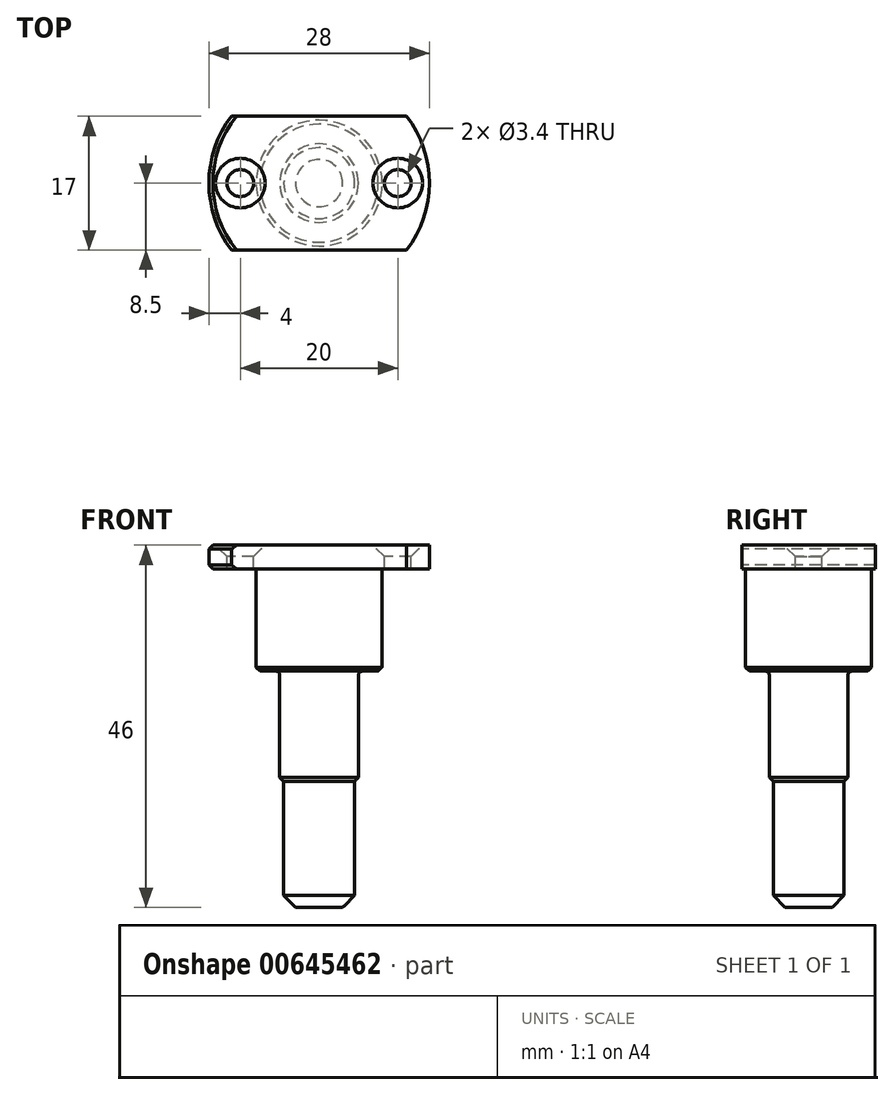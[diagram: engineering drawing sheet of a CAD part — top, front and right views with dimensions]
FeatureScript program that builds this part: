
annotation { "Feature Type Name" : "Feature", "Feature Type Description" : "" }
export const myFeature = defineFeature(function(context is Context, id is Id, definition is map)
    precondition{}
    {
        {
            var Q0;
            Q0=qCreatedBy(makeId("Top.planeOp"),FACE);
            var sketch = newSketch(context, id + "F0", { "sketchPlane" : qUnion([Q0])});
            skCircle(sketch, "E0", {"center": v(0, 0) * mm, "radius": 8 * mm});
            skSolve(sketch);
        }
        {
            var Q0;
            Q0=qCreatedBy(makeId("Top.planeOp"),FACE);
            var sketch = newSketch(context, id + "F1", { "sketchPlane" : qUnion([Q0])});
            skCircle(sketch, "E1", {"center": v(0, 0) * mm, "radius": 5 * mm});
            skSolve(sketch);
        }
        {
            var Q0;
            Q0=qCreatedBy(makeId("Top.planeOp"),FACE);
            var sketch = newSketch(context, id + "F2", { "sketchPlane" : qUnion([Q0])});
            skCircle(sketch, "E2", {"center": v(0, 0) * mm, "radius": 4.5 * mm});
            skSolve(sketch);
        }
        {
            var Q0;
            Q0 = qSketchRegion(id + "F2", true);
            extrude(context, id + "F3", {"entities" : qUnion([Q0]), "oppositeDirection" : true, "depth" : 46 * mm, "offsetDistance" : 25.4 * mm});
        }
        {
            var Q0;
            Q0 = qSketchRegion(id + "F1", true);
            extrude(context, id + "F4", {"entities" : qUnion([Q0]), "operationType" : NewBodyOperationType.ADD, "oppositeDirection" : true, "depth" : 30 * mm, "offsetDistance" : 25.4 * mm});
        }
        {
            var Q0;
            Q0 = qSketchRegion(id + "F0", true);
            extrude(context, id + "F5", {"entities" : qUnion([Q0]), "operationType" : NewBodyOperationType.ADD, "oppositeDirection" : true, "depth" : 16 * mm, "offsetDistance" : 25.4 * mm});
        }
        {
            var Q0;
            Q0=makeQuery(id+"F3.opExtrude","CAP_EDGE",EDGE,{"disambiguationData":[OSD([sQuery(id+"F2.wireOp",EDGE,"E2")])],"isStart":false});
            chamfer(context, id + "F6", {"entities" : qUnion([Q0]), "chamferType" : ChamferType.OFFSET_ANGLE, "width" : 1.5 * mm, "oppositeDirection" : false, "angle" : 45 * degree, "tangentPropagation" : true});
        }
        {
            var Q0;
            Q0=makeQuery(id+"F4.opExtrude","CAP_EDGE",EDGE,{"disambiguationData":[OSD([sQuery(id+"F1.wireOp",EDGE,"E1")])],"isStart":false});
            chamfer(context, id + "F7", {"entities" : qUnion([Q0]), "chamferType" : ChamferType.OFFSET_ANGLE, "width" : 0.5 * mm, "oppositeDirection" : false, "angle" : 45 * degree, "tangentPropagation" : true});
        }
        {
            var Q0;
            Q0=makeQuery(id+"F5.opExtrude","CAP_EDGE",EDGE,{"disambiguationData":[OSD([sQuery(id+"F0.wireOp",EDGE,"E0")])],"isStart":false});
            chamfer(context, id + "F8", {"entities" : qUnion([Q0]), "chamferType" : ChamferType.OFFSET_ANGLE, "width" : 0.5 * mm, "oppositeDirection" : false, "angle" : 45 * degree, "tangentPropagation" : true});
        }
        {
            var Q0;
            Q0=qCreatedBy(makeId("Top.planeOp"),FACE);
            var sketch = newSketch(context, id + "F9", { "sketchPlane" : qUnion([Q0])});
            skArc(sketch, "E3", {"start": v(-11.12, 8.5) * mm, "mid": v(-14, 0) * mm, "end": v(-11.12, -8.5) * mm});
            skLineSegment(sketch, "E4", {"start": v(-11.12, 8.5) * mm, "end": v(11.12, 8.5) * mm});
            skLineSegment(sketch, "E5", {"start": v(-11.12, -8.5) * mm, "end": v(11.12, -8.5) * mm});
            skArc(sketch, "E6.trimOffspring", {"start": v(11.12, -8.5) * mm, "mid": v(14, 0) * mm, "end": v(11.12, 8.5) * mm});
            skSolve(sketch);
        }
        {
            var Q0;
            Q0 = qSketchRegion(id + "F9", true);
            extrude(context, id + "F10", {"entities" : qUnion([Q0]), "operationType" : NewBodyOperationType.ADD, "oppositeDirection" : true, "depth" : 3 * mm, "offsetDistance" : 25.4 * mm});
        }
        {
            var Q0;
            Q0=makeQuery(id+"F9.imprint","IMPRINT",FACE,{"disambiguationData":[TD([[makeQuery(id+"F9.imprint","IMPRINT",EDGE,{"derivedFrom":sQuery(id+"F9.wireOp",EDGE,"E3")}),1.0]])]});
            var sketch = newSketch(context, id + "F11", { "sketchPlane" : qUnion([Q0])});
            skPoint(sketch, "E7", {"position": v(-10, 0) * mm});
            skPoint(sketch, "E8", {"position": v(10, 0) * mm});
            skSolve(sketch);
        }
        {
            var Q0;
            Q0=sQuery(id+"F11.wireOp",VERTEX,"E7");
            var Q1;
            Q1=makeQuery(id+"F3.opExtrude","SWEPT_BODY",BODY,{"disambiguationData":[OSD([sQuery(id+"F2.wireOp",EDGE,"E2")])]});
            hole(context, id + "F12", {"style" : HoleStyle.C_SINK, "endStyle" : HoleEndStyle.THROUGH, "holeDiameter" : 3.4 * mm, "cSinkDiameter" : 6.3 * mm, "cSinkAngle" : 90 * degree, "majorDiameter" : 6.35 * mm, "isTappedThrough" : true, "tappedDepth" : 12.7 * mm, "tapClearance" : 3, "locations" : qUnion([Q0]), "scope" : qUnion([Q1])});
        }
        {
            var Q0;
            Q0=sQuery(id+"F11.wireOp",VERTEX,"E8");
            var Q1;
            Q1=makeQuery(id+"F3.opExtrude","SWEPT_BODY",BODY,{"disambiguationData":[OSD([sQuery(id+"F2.wireOp",EDGE,"E2")])]});
            hole(context, id + "F13", {"style" : HoleStyle.C_SINK, "endStyle" : HoleEndStyle.THROUGH, "holeDiameter" : 3.4 * mm, "cSinkDiameter" : 6.3 * mm, "cSinkAngle" : 90 * degree, "majorDiameter" : 6.35 * mm, "isTappedThrough" : true, "tappedDepth" : 12.7 * mm, "tapClearance" : 3, "locations" : qUnion([Q0]), "scope" : qUnion([Q1])});
        }
        {
            var Q0;
            {var subQ0=sQuery(id+"F9.wireOp",EDGE,"E3");var subQ1=makeQuery(id+"F9.imprint","IMPRINT",EDGE,{"derivedFrom":subQ0});Q0=makeQuery(id+"F10.opExtrude","CAP_EDGE",EDGE,{"disambiguationData":[OSD([subQ0]),TDD([makeQuery(id+"FoYEAjmDboDuPMb_1.imprint","IMPRINT",EDGE,{"disambiguationData":[TD([[makeQuery(id+"FoYEAjmDboDuPMb_1.imprint","INTERSECT",VERTEX,{"disambiguationData":[OD(1.0)],"derivedFrom":[subQ1,sQuery(id+"FoYEAjmDboDuPMb_1.wireOp",EDGE,"zp1TZnEM-hQR9-ePwr-UHcE-iEev8KjVGf00")]}),1.0]])],"derivedFrom":subQ1})])],"isStart":false});}
            var Q1;
            Q1=makeQuery(id+"F10.opExtrude","CAP_EDGE",EDGE,{"disambiguationData":[OSD([sQuery(id+"FoYEAjmDboDuPMb_1.wireOp",EDGE,"zp1TZnEM-hQR9-ePwr-UHcE-iEev8KjVGf00")])],"isStart":false});
            var Q2;
            {var subQ0=sQuery(id+"F9.wireOp",EDGE,"E3");var subQ1=makeQuery(id+"F9.imprint","IMPRINT",EDGE,{"derivedFrom":subQ0});Q2=makeQuery(id+"F10.opExtrude","CAP_EDGE",EDGE,{"disambiguationData":[OSD([subQ0]),TDD([makeQuery(id+"FoYEAjmDboDuPMb_1.imprint","IMPRINT",EDGE,{"disambiguationData":[TD([[makeQuery(id+"FoYEAjmDboDuPMb_1.imprint","INTERSECT",VERTEX,{"disambiguationData":[OD(0.0)],"derivedFrom":[subQ1,sQuery(id+"FoYEAjmDboDuPMb_1.wireOp",EDGE,"zp1TZnEM-hQR9-ePwr-UHcE-iEev8KjVGf00")]}),-1.0]])],"derivedFrom":subQ1})])],"isStart":false});}
            var Q3;
            Q3=makeQuery(id+"F10.opExtrude","CAP_EDGE",EDGE,{"disambiguationData":[OSD([sQuery(id+"FoYEAjmDboDuPMb_1.wireOp",EDGE,"0RWUmBst-VcDq-Yw5Y-qvDI-bN0Ma2whnU3Y")])],"isStart":false});
            var Q4;
            Q4=makeQuery(id+"F10.opExtrude","CAP_EDGE",EDGE,{"disambiguationData":[OSD([sQuery(id+"FoYEAjmDboDuPMb_1.wireOp",EDGE,"0RWUmBst-VcDq-Yw5Y-qvDI-bN0Ma2whnU3Y")])],"isStart":true});
            var Q5;
            {var subQ0=sQuery(id+"F9.wireOp",EDGE,"E3");var subQ1=makeQuery(id+"F9.imprint","IMPRINT",EDGE,{"derivedFrom":subQ0});Q5=makeQuery(id+"F10.opExtrude","CAP_EDGE",EDGE,{"disambiguationData":[OSD([subQ0]),TDD([makeQuery(id+"FoYEAjmDboDuPMb_1.imprint","IMPRINT",EDGE,{"disambiguationData":[TD([[makeQuery(id+"FoYEAjmDboDuPMb_1.imprint","INTERSECT",VERTEX,{"disambiguationData":[OD(0.0)],"derivedFrom":[subQ1,sQuery(id+"FoYEAjmDboDuPMb_1.wireOp",EDGE,"zp1TZnEM-hQR9-ePwr-UHcE-iEev8KjVGf00")]}),-1.0]])],"derivedFrom":subQ1})])],"isStart":true});}
            var Q6;
            {var subQ0=sQuery(id+"F9.wireOp",EDGE,"E3");var subQ1=makeQuery(id+"F9.imprint","IMPRINT",EDGE,{"derivedFrom":subQ0});Q6=makeQuery(id+"F10.opExtrude","CAP_EDGE",EDGE,{"disambiguationData":[OSD([subQ0]),TDD([makeQuery(id+"FoYEAjmDboDuPMb_1.imprint","IMPRINT",EDGE,{"disambiguationData":[TD([[makeQuery(id+"FoYEAjmDboDuPMb_1.imprint","INTERSECT",VERTEX,{"disambiguationData":[OD(1.0)],"derivedFrom":[subQ1,sQuery(id+"FoYEAjmDboDuPMb_1.wireOp",EDGE,"zp1TZnEM-hQR9-ePwr-UHcE-iEev8KjVGf00")]}),1.0]])],"derivedFrom":subQ1})])],"isStart":true});}
            var Q7;
            Q7=makeQuery(id+"F10.opExtrude","CAP_EDGE",EDGE,{"disambiguationData":[OSD([sQuery(id+"FoYEAjmDboDuPMb_1.wireOp",EDGE,"zp1TZnEM-hQR9-ePwr-UHcE-iEev8KjVGf00")])],"isStart":true});
            chamfer(context, id + "F14", {"entities" : qUnion([Q0, Q1, Q2, Q3, Q4, Q5, Q6, Q7]), "chamferType" : ChamferType.OFFSET_ANGLE, "width" : 0.5 * mm, "oppositeDirection" : false, "angle" : 45 * degree, "tangentPropagation" : true});
        }
        {
            var Q0;
            Q0=makeQuery(id+"F5.boolean.opBoolean","INTERSECT",EDGE,{"derivedFrom":[makeQuery(id+"F4.opExtrude","SWEPT_FACE",FACE,{"disambiguationData":[OSD([sQuery(id+"F1.wireOp",EDGE,"E1")])]}),makeQuery(id+"F5.opExtrude","CAP_FACE",FACE,{"disambiguationData":[OSD([sQuery(id+"F0.wireOp",EDGE,"E0")])],"isStart":false})]});
            fillet(context, id + "F15", {"entities" : qUnion([Q0]), "radius" : 0.5 * mm, "tangentPropagation" : true, "allowEdgeOverflow" : false});
        }
    });
